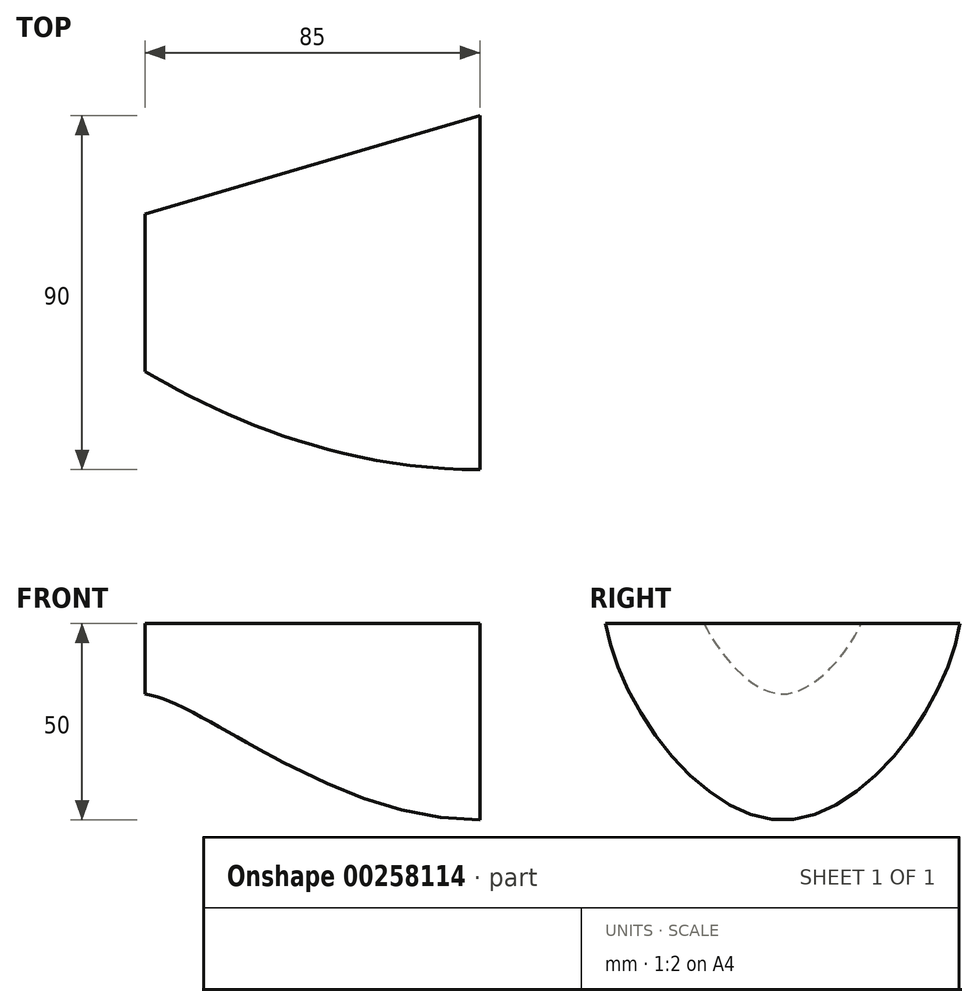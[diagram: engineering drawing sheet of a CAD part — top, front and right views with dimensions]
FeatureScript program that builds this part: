
annotation { "Feature Type Name" : "Feature", "Feature Type Description" : "" }
export const myFeature = defineFeature(function(context is Context, id is Id, definition is map)
    precondition{}
    {
        {
            var Q0;
            Q0=qCreatedBy(makeId("Right.planeOp"),FACE);
            cPlane(context, id + "F0", {"entities" : qUnion([Q0]), "cplaneType" : CPlaneType.OFFSET, "offset" : 85 * mm, "oppositeDirection" : true, "width" : 150 * mm, "height" : 150 * mm});
        }
        {
            var Q0;
            Q0=qCreatedBy(makeId("Right.planeOp"),FACE);
            var sketch = newSketch(context, id + "F1", { "sketchPlane" : qUnion([Q0])});
            skFitSpline(sketch, "E0", {"points": [v(-45, 0) * mm, v(0, -50) * mm, v(45, 0) * mm], "startDerivative": vector(18, -120) * mm, "endDerivative": vector(18, 120) * mm});
            skLineSegment(sketch, "E1", {"start": v(-45, 0) * mm, "end": v(45, 0) * mm});
            skSolve(sketch);
        }
        {
            var Q0;
            Q0=qCreatedBy(id+"F0.planeOp",FACE);
            var sketch = newSketch(context, id + "F2", { "sketchPlane" : qUnion([Q0])});
            skFitSpline(sketch, "E2", {"points": [v(-20, 0) * mm, v(0, -18) * mm, v(20, 0) * mm], "startDerivative": vector(12, -30) * mm, "endDerivative": vector(12, 30) * mm});
            skFitSpline(sketch, "E3", {"points": [v(20, 0) * mm, v(-20, 0) * mm], "startDerivative": vector(-40, 0) * mm, "endDerivative": vector(-40, 0) * mm});
            skSolve(sketch);
        }
        {
            var Q0;
            Q0=qCreatedBy(makeId("Top.planeOp"),FACE);
            var sketch = newSketch(context, id + "F3", { "sketchPlane" : qUnion([Q0])});
            skPoint(sketch, "E4.0", {"position": v(0, -45) * mm});
            skPoint(sketch, "E5.0", {"position": v(-85, -20) * mm});
            skLineSegment(sketch, "E6.0", {"start": v(0, -45) * mm, "end": v(0, 45) * mm});
            skFitSpline(sketch, "E7.0", {"points": [v(0, -45) * mm, v(0, -42) * mm, v(0, 0) * mm, v(0, 42) * mm, v(0, 45) * mm]});
            skFitSpline(sketch, "E8", {"points": [v(-85, -20) * mm, v(0, -45) * mm], "startDerivative": vector(60, -36) * mm, "endDerivative": vector(105, 0) * mm});
            skPoint(sketch, "E9.0", {"position": v(-85, 20) * mm});
            skFitSpline(sketch, "E10.0", {"points": [v(0, -45) * mm, v(0, -42) * mm, v(0, 0) * mm, v(0, 42) * mm, v(0, 45) * mm]});
            skFitSpline(sketch, "E11.0", {"points": [v(0, -45) * mm, v(0, -42) * mm, v(0, 0) * mm, v(0, 42) * mm, v(0, 45) * mm]});
            skFitSpline(sketch, "E12", {"points": [v(-85, 20) * mm, v(0, 45) * mm], "startDerivative": vector(60, 36) * mm, "endDerivative": vector(105, 0) * mm});
            skSolve(sketch);
        }
        {
            var Q0;
            Q0=qCreatedBy(makeId("Front.planeOp"),FACE);
            var sketch = newSketch(context, id + "F4", { "sketchPlane" : qUnion([Q0])});
            skFitSpline(sketch, "E13", {"points": [v(-85, -18) * mm, v(0, -50) * mm], "startDerivative": vector(45, -6) * mm, "endDerivative": vector(113.52, 0) * mm});
            skSolve(sketch);
        }
        {
            var Q0;
            Q0=makeQuery(id+"F1.imprint","IMPRINT",FACE,{"disambiguationData":[TD([[makeQuery(id+"F1.imprint","IMPRINT",EDGE,{"derivedFrom":sQuery(id+"F1.wireOp",EDGE,"E0")}),1.0]])]});
            var Q1;
            Q1=makeQuery(id+"F2.imprint","IMPRINT",FACE,{"disambiguationData":[TD([[makeQuery(id+"F2.imprint","IMPRINT",EDGE,{"derivedFrom":sQuery(id+"F2.wireOp",EDGE,"E2")}),1.0]])]});
            var Q2;
            Q2=sQuery(id+"F4.wireOp",EDGE,"E13");
            var Q3;
            Q3=sQuery(id+"F3.wireOp",EDGE,"E8");
            loft(context, id + "F5", {"addGuides" : true, "sheetProfilesArray" : [{ "sheetProfileEntities" : qUnion([Q0]) }, { "sheetProfileEntities" : qUnion([Q1]) }], "guidesArray" : [{ "guideEntities" : qUnion([Q2]), "guideDerivativeType" : LoftGuideDerivativeType.DEFAULT, "guideDerivativeMagnitude" : 1 }, { "guideEntities" : qUnion([Q3]), "guideDerivativeType" : LoftGuideDerivativeType.DEFAULT, "guideDerivativeMagnitude" : 1 }]});
        }
    });
